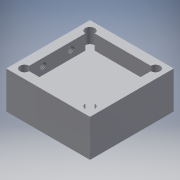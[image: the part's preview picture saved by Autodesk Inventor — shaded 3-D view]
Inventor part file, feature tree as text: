
AUTODESK INVENTOR PART (.ipt)
format: ipt  version: 2016 (Build 200138000, 138)  size: 164,352 bytes
history: native  units: mm
features: sketch x7, hole x4, extrude x3, projected_geometry x3
ambient origin geometry x8: Origin, YZ Plane, XZ Plane, XY Plane, X Axis, Y Axis, Z Axis, Center Point
bodies: Solid1 (feature_tree)
feature tree (17):
  extrude  "Extrusion1"  Depth=45.0mm
  hole  "Hole2"  [1 undecoded]
  extrude  "Extrusion3"  Depth=8.0mm TaperAngle=0.0deg
  hole  "Hole3"  [1 undecoded]
  extrude  "Extrusion4"  Depth=25.0mm
  hole  "Hole5"  [1 undecoded]
  hole  "Hole6"  [1 undecoded]
  sketch  "Sketch1"  dims[d0=45.0mm d1=45.0mm]
  sketch  "Sketch4"  dims[d2=20.0mm d3=0.0mm d15=35.15mm]
  sketch  "Sketch5"  dims[d16=35.15mm]
  sketch  "Sketch6"  dims[d17=5.0mm d18=6.0mm d19=4.0mm d20=2.0mm d21=90.0deg d22=8.0mm d23=0.0mm d24=8.0mm d25=0.0mm]
  projected_geometry  "Projected Loop1"
  sketch  "Sketch8"  dims[d26=15.0mm d27=15.0mm]
  projected_geometry  "Projected Loop2"
  sketch  "Sketch9"  dims[d28=3.242mm d29=6.0mm d30=4.0mm d31=2.0mm d32=90.0deg d33=8.0mm d34=20.594885mm d44=25.0mm]
  projected_geometry  "Projected Loop3"
  sketch  "Sketch10"  dims[d45=25.0mm d46=6.0mm d47=0.0mm d48=3.0mm d49=6.0mm d50=4.0mm d51=2.0mm d52=90.0deg d53=6.0mm d54=0.0mm d55=3.242mm d56=8.0mm d57=4.0mm d58=2.0mm d59=90.0deg d60=4.0mm d61=20.594885mm]
note: 4 required parameter values undecoded (feature->parameter linkage not recoverable at this tier; creation-order binding heuristic only, values carry confidence <= 0.55)
